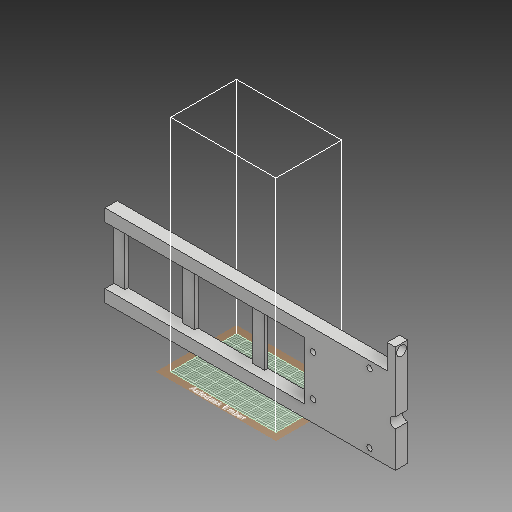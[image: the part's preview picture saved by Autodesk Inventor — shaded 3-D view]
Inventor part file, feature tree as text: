
AUTODESK INVENTOR PART (.ipt)
format: ipt  version: 2018 (Build 220112000, 112)  size: 1,123,840 bytes
history: native  units: mm
features: sketch x80, extrude x63, fillet x22, hole x8
ambient origin geometry x8: Origin, YZ Plane, XZ Plane, XY Plane, X Axis, Y Axis, Z Axis, Center Point
bodies: Solid1 (feature_tree)
feature tree (173):
  extrude  "Extrusion1"  Depth=50.0mm
  hole  "Hole1"  [1 undecoded]
  hole  "Hole2"  [1 undecoded]
  extrude  "Extrusion2"  Depth=25.0mm
  extrude  "Extrusion3"  Depth=25.0mm
  extrude  "Extrusion4"  Depth=5.0mm
  sketch  "Sketch7"  dims[d25=10.0mm d26=5.0mm]
  extrude  "Extrusion5"  Depth=5.0mm
  extrude  "Extrusion6"  Depth=35.0mm
  extrude  "Extrusion7"  Depth=35.0mm
  extrude  "Extrusion8"  Depth=35.0mm
  extrude  "Extrusion9"  Depth=2.0mm TaperAngle=0.0deg
  extrude  "Extrusion10"  Depth=7.5mm TaperAngle=0.0deg
  extrude  "Extrusion11"  Depth=10.0mm
  extrude  "Extrusion12"  Depth=7.5mm
  fillet  "Fillet1"  Radius=7.5mm
  fillet  "Fillet2"  Radius=25.0mm
  fillet  "Fillet3"  Radius=3.0mm
  fillet  "Fillet4"  Radius=3.2mm
  fillet  "Fillet5"  Radius=2.1mm
  fillet  "Fillet6"  Radius=5.5mm
  extrude  "Extrusion13"  Depth=92.5mm TaperAngle=0.0deg
  sketch  "Sketch17"  dims[d58=4.25mm d59=241.0mm d60=0.0mm]
  hole  "Hole3"  [1 undecoded]
  hole  "Hole4"  [1 undecoded]
  extrude  "Extrusion14"  Depth=5.0mm
  extrude  "Extrusion15"  Depth=2.5mm TaperAngle=0.0deg
  extrude  "Extrusion16"  Depth=6.35mm
  extrude  "Extrusion17"  Depth=2.5mm
  extrude  "Extrusion18"  Depth=14.55mm TaperAngle=0.0deg
  extrude  "Extrusion19"  Depth=0.1mm
  extrude  "Extrusion20"  Depth=3.25mm
  extrude  "Extrusion21"  Depth=3.25mm
  hole  "Hole5"  [1 undecoded]
  extrude  "Extrusion22"  Depth=2.0mm
  extrude  "Extrusion23"  Depth=15.0mm
  extrude  "Extrusion24"  Depth=10.0mm TaperAngle=0.0deg
  hole  "Hole6"  [1 undecoded]
  extrude  "Extrusion25"  Depth=100.0mm TaperAngle=0.0deg
  extrude  "Extrusion26"  Depth=2.0mm TaperAngle=0.0deg
  extrude  "Extrusion27"  Depth=3.3mm
  extrude  "Extrusion28"  Depth=3.3mm
  hole  "Hole7"  [1 undecoded]
  extrude  "Extrusion29"  Depth=8.0mm
  extrude  "Extrusion30"  Depth=17.0mm
  hole  "Hole8"  [1 undecoded]
  extrude  "Extrusion31"  Depth=3.5mm
  extrude  "Extrusion32"  Depth=10.0mm
  fillet  "Fillet7"  Radius=3.3mm
  fillet  "Fillet8"  Radius=10.0mm
  extrude  "Extrusion33"  Depth=5.0mm
  extrude  "Extrusion34"  Depth=5.0mm
  sketch  "Sketch45"  dims[d149=10.0mm d150=17.5mm d151=0.0mm]
  sketch  "Sketch46"  dims[d152=5.0mm]
  extrude  "Extrusion35"  Depth=10.0mm TaperAngle=0.0deg
  extrude  "Extrusion36"  Depth=8.0mm TaperAngle=0.0deg
  extrude  "Extrusion37"  Depth=3.75mm
  extrude  "Extrusion38"  Depth=3.75mm
  extrude  "Extrusion39"  Depth=10.0mm TaperAngle=0.0deg
  extrude  "Extrusion40"  Depth=2.0mm TaperAngle=0.0deg
  fillet  "Fillet9"  Radius=5.0mm
  fillet  "Fillet10"  Radius=15.0mm
  fillet  "Fillet11"  Radius=7.5mm
  fillet  "Fillet12"  Radius=17.5mm
  extrude  "Extrusion41"  Depth=47.5mm
  extrude  "Extrusion42"  Depth=5.0mm
  sketch  "Sketch55"  dims[d200=20.0mm d203=5.0mm]
  extrude  "Extrusion43"  Depth=5.0mm
  extrude  "Extrusion44"  Depth=7.5mm TaperAngle=0.0deg
  extrude  "Extrusion45"  Depth=4.0mm
  extrude  "Extrusion46"  Depth=12.0mm
  extrude  "Extrusion47"  Depth=7.5mm
  extrude  "Extrusion48"  Depth=20.0mm TaperAngle=0.0deg
  extrude  "Extrusion49"  Depth=20.0mm
  extrude  "Extrusion50"  Depth=4.0mm
  extrude  "Extrusion51"  Depth=10.0mm TaperAngle=0.0deg
  extrude  "Extrusion52"  Depth=5.5mm TaperAngle=0.0deg
  fillet  "Fillet13"  Radius=10.0mm
  fillet  "Fillet14"  Radius=74.724mm
  fillet  "Fillet15"  Radius=74.724mm
  fillet  "Fillet16"  Radius=85.515mm
  extrude  "Extrusion53"  Depth=5.0mm
  extrude  "Extrusion54"  Depth=5.0mm
  fillet  "Fillet17"  Radius=85.515mm
  extrude  "Extrusion55"  Depth=2.0mm TaperAngle=0.0deg
  fillet  "Fillet18"  Radius=2.0mm
  extrude  "Extrusion56"  Depth=2.0mm
  sketch  "Sketch70"  dims[d247=2.0mm d248=10.0mm d249=2.0mm d250=0.0mm d251=1.0mm d252=0.0mm]
  extrude  "Extrusion57"  Depth=10.0mm
  fillet  "Fillet19"  Radius=2.0mm
  fillet  "Fillet20"  Radius=1.0mm
  extrude  "Extrusion58"  Depth=1.0mm TaperAngle=0.0deg
  extrude  "Extrusion59"  Depth=0.349066mm
  fillet  "Fillet21"  Radius=0.349066mm
  sketch  "Sketch74"  dims[d262=4.0mm d263=10.0mm d264=0.0mm]
  extrude  "Extrusion60"  Depth=4.0mm
  sketch  "Sketch76"  dims[d270=3.0mm d271=24.5mm]
  extrude  "Extrusion61"  Depth=10.0mm TaperAngle=0.0deg
  extrude  "Extrusion62"  Depth=6.5mm
  fillet  "Fillet22"  Radius=5.5mm
  sketch  "Sketch79"  dims[d276=24.5mm]
  extrude  "Extrusion63"  Depth=24.5mm
  sketch  "Sketch1"  dims[d0=50.0mm d1=50.0mm]
  sketch  "Sketch2"  dims[d2=240.0mm d3=7.5mm]
  sketch  "Sketch3"  dims[d4=7.5mm d5=7.5mm d6=0.0mm]
  sketch  "Sketch4"  dims[d7=6.35mm d8=6.0mm d9=4.0mm d10=2.0mm d11=90.0deg d12=8.0mm d13=20.594885mm d14=25.0mm]
  sketch  "Sketch5"  dims[d15=3.3mm d16=6.0mm d17=4.0mm d18=2.0mm d19=90.0deg d20=8.0mm d21=20.594885mm d22=25.0mm]
  sketch  "Sketch6"  dims[d23=180.0deg d24=5.0mm]
  sketch  "Sketch8"  dims[d27=17.5mm d28=0.0mm d30=35.0mm]
  sketch  "Sketch9"  dims[d31=35.0mm d32=35.0mm]
  sketch  "Sketch10"  dims[d33=35.0mm d34=35.0mm]
  sketch  "Sketch11"  dims[d35=35.0mm d36=2.0mm d37=0.0mm]
  sketch  "Sketch12"  dims[d38=10.0mm d39=7.5mm d40=0.0mm]
  sketch  "Sketch13"  dims[d41=100.0mm d42=10.0mm]
  sketch  "Sketch14"  dims[d43=7.5mm d44=0.0mm d45=7.5mm d46=7.5mm d47=25.0mm d48=0.0mm d49=3.0mm d50=3.2mm d51=2.1mm d52=5.5mm]
  sketch  "Sketch15"  dims[d53=3.3mm d54=92.5mm d55=0.0mm]
  sketch  "Sketch16"  dims[d56=5.5mm d57=3.3mm]
  sketch  "Sketch18"  dims[d61=4.44mm d62=5.0mm]
  sketch  "Sketch19"  dims[d63=2.5mm d64=91.25mm d65=0.0mm]
  sketch  "Sketch20"  dims[d66=30.0mm d67=6.35mm]
  sketch  "Sketch21"  dims[d68=3.8mm d69=0.0mm d70=2.5mm]
  sketch  "Sketch22"  dims[d71=14.55mm d72=0.0mm d73=14.55mm d74=0.0mm]
  sketch  "Sketch23"  dims[d75=0.1mm d76=0.1mm]
  sketch  "Sketch24"  dims[d77=3.25mm d78=3.25mm]
  sketch  "Sketch25"  dims[d79=3.25mm d80=3.25mm]
  sketch  "Sketch26"  dims[d81=35.0mm d82=10.0mm]
  sketch  "Sketch27"  dims[d83=2.0mm d84=0.0mm d85=3.6mm]
  sketch  "Sketch28"  dims[d86=3.6mm]
  sketch  "Sketch29"  dims[d87=3.3mm d88=6.0mm d89=4.0mm d90=2.0mm d91=90.0deg d92=15.0mm d93=20.594885mm]
  sketch  "Sketch30"  dims[d94=3.3mm d95=6.0mm d96=4.0mm d97=2.0mm d98=90.0deg d99=15.0mm d100=20.594885mm d101=6.0mm]
  sketch  "Sketch31"  dims[d102=20.0mm d103=0.0mm d104=10.0mm d105=0.0mm]
  sketch  "Sketch32"  dims[d106=2.0mm d107=0.0mm d108=4.0mm]
  sketch  "Sketch33"  dims[d109=100.0mm d110=0.0mm d111=100.0mm d112=0.0mm]
  sketch  "Sketch34"  dims[d113=5.0mm d114=2.0mm d115=0.0mm]
  sketch  "Sketch35"  dims[d116=3.3mm d117=3.3mm]
  sketch  "Sketch36"  dims[d118=3.3mm d119=3.3mm]
  sketch  "Sketch37"  dims[d120=2.0mm d121=0.0mm d122=5.5mm d123=0.0mm]
  sketch  "Sketch38"  dims[d124=3.3mm d125=6.0mm d126=4.0mm d127=2.0mm d128=90.0deg d129=8.0mm d130=20.594885mm d131=42.0mm]
  sketch  "Sketch39"  dims[d132=17.0mm d133=21.0mm]
  sketch  "Sketch40"  dims[d135=8.5mm d136=15.825mm]
  sketch  "Sketch41"  dims[d137=3.5mm d138=21.0mm]
  sketch  "Sketch42"  dims[d139=3.3mm d140=3.3mm d141=3.3mm d142=10.0mm d143=0.0mm]
  sketch  "Sketch43"  dims[d144=7.5mm d145=0.0mm d146=5.0mm]
  sketch  "Sketch44"  dims[d147=10.0mm d148=5.0mm]
  sketch  "Sketch47"  dims[d153=7.0mm d154=6.0mm d155=4.0mm d156=2.0mm d157=90.0deg d158=8.0mm d159=20.594885mm d160=17.5mm d161=0.0mm]
  sketch  "Sketch48"  dims[d162=170.5mm d163=0.0mm d164=3.75mm]
  sketch  "Sketch49"  dims[d165=3.75mm d166=3.75mm]
  sketch  "Sketch50"  dims[d167=3.75mm d168=10.0mm d169=0.0mm]
  sketch  "Sketch51"  dims[d170=100.0mm d171=0.0mm]
  sketch  "Sketch52"  dims[d172=5.0mm d173=6.0mm d174=4.0mm d175=2.0mm d176=90.0deg d177=15.0mm d178=0.0mm d179=2.0mm d180=0.0mm d181=5.0mm d182=15.0mm d183=0.0mm d184=7.5mm]
  sketch  "Sketch53"  dims[d185=6.0mm d186=6.0mm d187=4.0mm d188=2.0mm d189=90.0deg d190=15.0mm d191=0.0mm d192=17.5mm d193=0.0mm]
  sketch  "Sketch54"  dims[d194=23.75mm d195=47.5mm]
  sketch  "Sketch56"  dims[d204=5.0mm d205=29.0mm]
  sketch  "Sketch57"  dims[d206=29.0mm d207=7.5mm d208=0.0mm]
  sketch  "Sketch58"  dims[d209=4.0mm d210=4.0mm]
  sketch  "Sketch59"  dims[d211=2.0mm d212=0.0mm d213=12.0mm]
  sketch  "Sketch60"  dims[d214=2.0mm d215=0.0mm d216=7.5mm]
  sketch  "Sketch61"  dims[d217=7.5mm d218=20.0mm d219=0.0mm]
  sketch  "Sketch62"  dims[d220=20.0mm d221=3.3mm]
  sketch  "Sketch63"  dims[d222=20.0mm d223=0.0mm d224=4.0mm]
  sketch  "Sketch64"  dims[d225=4.0mm d226=10.0mm d227=0.0mm]
  sketch  "Sketch65"  dims[d228=3.0mm d229=5.5mm d230=0.0mm d231=10.0mm d232=0.0mm d233=74.724mm d234=74.724mm d235=85.515mm]
  sketch  "Sketch66"  dims[d236=5.0mm d237=5.0mm]
  sketch  "Sketch67"  dims[d238=85.515mm d239=5.0mm d240=85.515mm]
  sketch  "Sketch68"  dims[d241=5.0mm d242=2.0mm d243=0.0mm d244=2.0mm]
  sketch  "Sketch69"  dims[d245=2.0mm d246=2.0mm]
  sketch  "Sketch71"  dims[d253=20.0mm d254=1.0mm d255=0.0mm]
  sketch  "Sketch72"  dims[d256=0.5mm d257=0.0mm d258=0.349066mm d259=0.349066mm]
  sketch  "Sketch73"  dims[d260=4.0mm d261=4.0mm]
  sketch  "Sketch75"  dims[d265=5.5mm d266=0.0mm d267=6.5mm d268=5.5mm d269=0.0mm]
  sketch  "Sketch77"  dims[d272=5500.0mm d273=0.0mm]
  sketch  "Sketch78"  dims[d274=5500.0mm d275=0.0mm]
  sketch  "Sketch80"  dims[d277=7.5mm d278=0.0mm d279=7.5mm d280=0.0mm d281=7.5mm d282=0.0mm d283=2.0mm d284=2.0mm d285=4.0mm d286=1.5mm d287=4.25mm d288=4.25mm d289=7.5mm d290=0.0mm d291=20.025mm d292=10.0mm d293=2.5mm d294=17.0mm d295=0.0mm d296=1.5mm d298=3.0mm d300=3.0mm d301=5.0mm d302=0.0mm d303=1.0mm d304=10.0mm d305=0.0mm d306=8.45mm d307=8.45mm d308=5.5mm d309=9.5mm d310=17.0mm d311=0.0mm d312=2.0mm d313=2.0mm d314=5.5mm d315=0.0mm d316=9.5mm d317=0.0mm d318=2.0mm d321=4.5mm d322=17.0mm d323=0.0mm d324=11.5mm d325=2.88mm d326=2.88mm d327=3.0mm d328=3.0mm d329=2.5mm d330=0.0mm d331=3.0mm d332=2.5mm d333=0.0mm d334=1.0mm d335=11.0mm d336=4.75mm d337=2.0mm d338=0.0mm]
note: 8 required parameter values undecoded (feature->parameter linkage not recoverable at this tier; creation-order binding heuristic only, values carry confidence <= 0.55)
